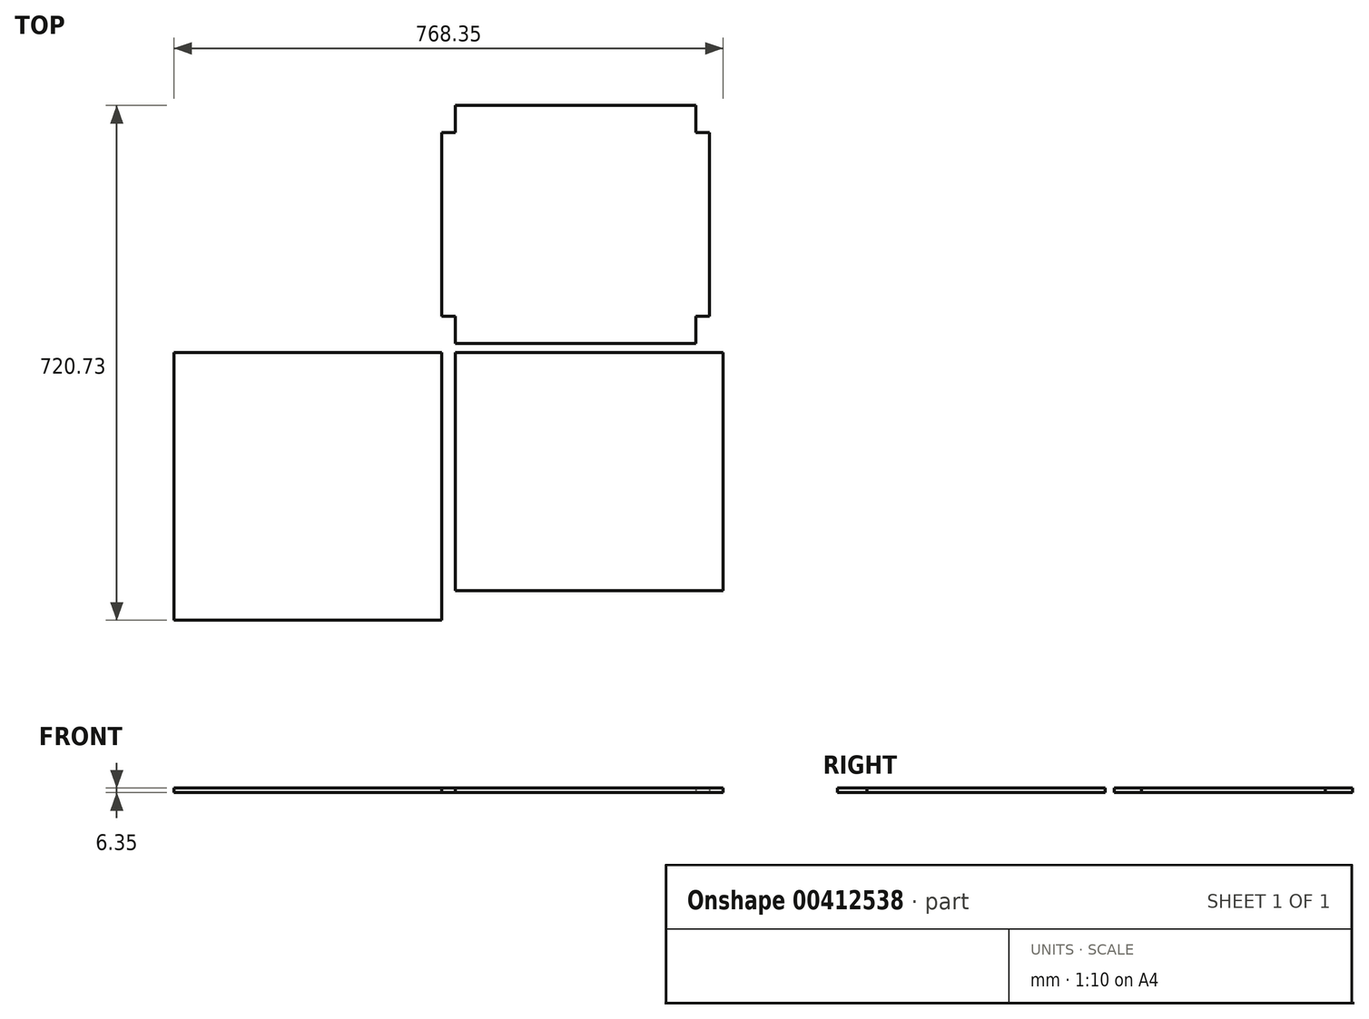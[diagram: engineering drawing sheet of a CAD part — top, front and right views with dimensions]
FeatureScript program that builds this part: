
annotation { "Feature Type Name" : "Feature", "Feature Type Description" : "" }
export const myFeature = defineFeature(function(context is Context, id is Id, definition is map)
    precondition{}
    {
        {
            var Q0;
            Q0=qCreatedBy(makeId("Top.planeOp"),FACE);
            var sketch = newSketch(context, id + "F0", { "sketchPlane" : qUnion([Q0])});
            skLineSegment(sketch, "E0", {"start": v(0, 0) * mm, "end": v(0, 38.1) * mm});
            skLineSegment(sketch, "E1", {"start": v(0, 38.1) * mm, "end": v(-19.05, 38.1) * mm});
            skLineSegment(sketch, "E2", {"start": v(-19.05, 38.1) * mm, "end": v(-19.05, 295.27) * mm});
            skLineSegment(sketch, "E3", {"start": v(-19.05, 295.28) * mm, "end": v(0, 295.28) * mm});
            skLineSegment(sketch, "E4", {"start": v(0, 295.27) * mm, "end": v(0, 333.37) * mm});
            skLineSegment(sketch, "E5", {"start": v(0, 333.38) * mm, "end": v(336.55, 333.38) * mm});
            skLineSegment(sketch, "E6", {"start": v(336.55, 333.38) * mm, "end": v(336.55, 295.28) * mm});
            skLineSegment(sketch, "E7", {"start": v(336.55, 295.28) * mm, "end": v(355.6, 295.28) * mm});
            skLineSegment(sketch, "E8", {"start": v(355.6, 295.28) * mm, "end": v(355.6, 38.1) * mm});
            skLineSegment(sketch, "E9", {"start": v(355.6, 38.1) * mm, "end": v(336.55, 38.1) * mm});
            skLineSegment(sketch, "E10", {"start": v(336.55, 38.1) * mm, "end": v(336.55, 0) * mm});
            skLineSegment(sketch, "E11", {"start": v(336.55, 0) * mm, "end": v(0, 0) * mm});
            skSolve(sketch);
        }
        {
            var Q0;
            Q0 = qSketchRegion(id + "F0", true);
            extrude(context, id + "F1", {"entities" : qUnion([Q0]), "depth" : 6.35 * mm});
        }
        {
            var Q0;
            Q0=qCreatedBy(makeId("Top.planeOp"),FACE);
            var sketch = newSketch(context, id + "F2", { "sketchPlane" : qUnion([Q0])});
            skLineSegment(sketch, "E12.bottom", {"start": v(0, -12.7) * mm, "end": v(374.65, -12.7) * mm});
            skLineSegment(sketch, "E12.top", {"start": v(0, -346.07) * mm, "end": v(374.65, -346.07) * mm});
            skLineSegment(sketch, "E12.left", {"start": v(0, -12.7) * mm, "end": v(0, -346.07) * mm});
            skLineSegment(sketch, "E12.right", {"start": v(374.65, -12.7) * mm, "end": v(374.65, -346.07) * mm});
            skSolve(sketch);
        }
        {
            var Q0;
            Q0 = qSketchRegion(id + "F2", true);
            extrude(context, id + "F3", {"entities" : qUnion([Q0]), "depth" : 6.35 * mm});
        }
        {
            var Q0;
            Q0=qCreatedBy(makeId("Top.planeOp"),FACE);
            var sketch = newSketch(context, id + "F4", { "sketchPlane" : qUnion([Q0])});
            skLineSegment(sketch, "E13.bottom", {"start": v(-19.05, -12.7) * mm, "end": v(-393.7, -12.7) * mm});
            skLineSegment(sketch, "E13.top", {"start": v(-19.05, -387.35) * mm, "end": v(-393.7, -387.35) * mm});
            skLineSegment(sketch, "E13.left", {"start": v(-19.05, -12.7) * mm, "end": v(-19.05, -387.35) * mm});
            skLineSegment(sketch, "E13.right", {"start": v(-393.7, -12.7) * mm, "end": v(-393.7, -387.35) * mm});
            skSolve(sketch);
        }
        {
            var Q0;
            Q0 = qSketchRegion(id + "F4", true);
            extrude(context, id + "F5", {"entities" : qUnion([Q0]), "depth" : 6.35 * mm});
        }
    });
